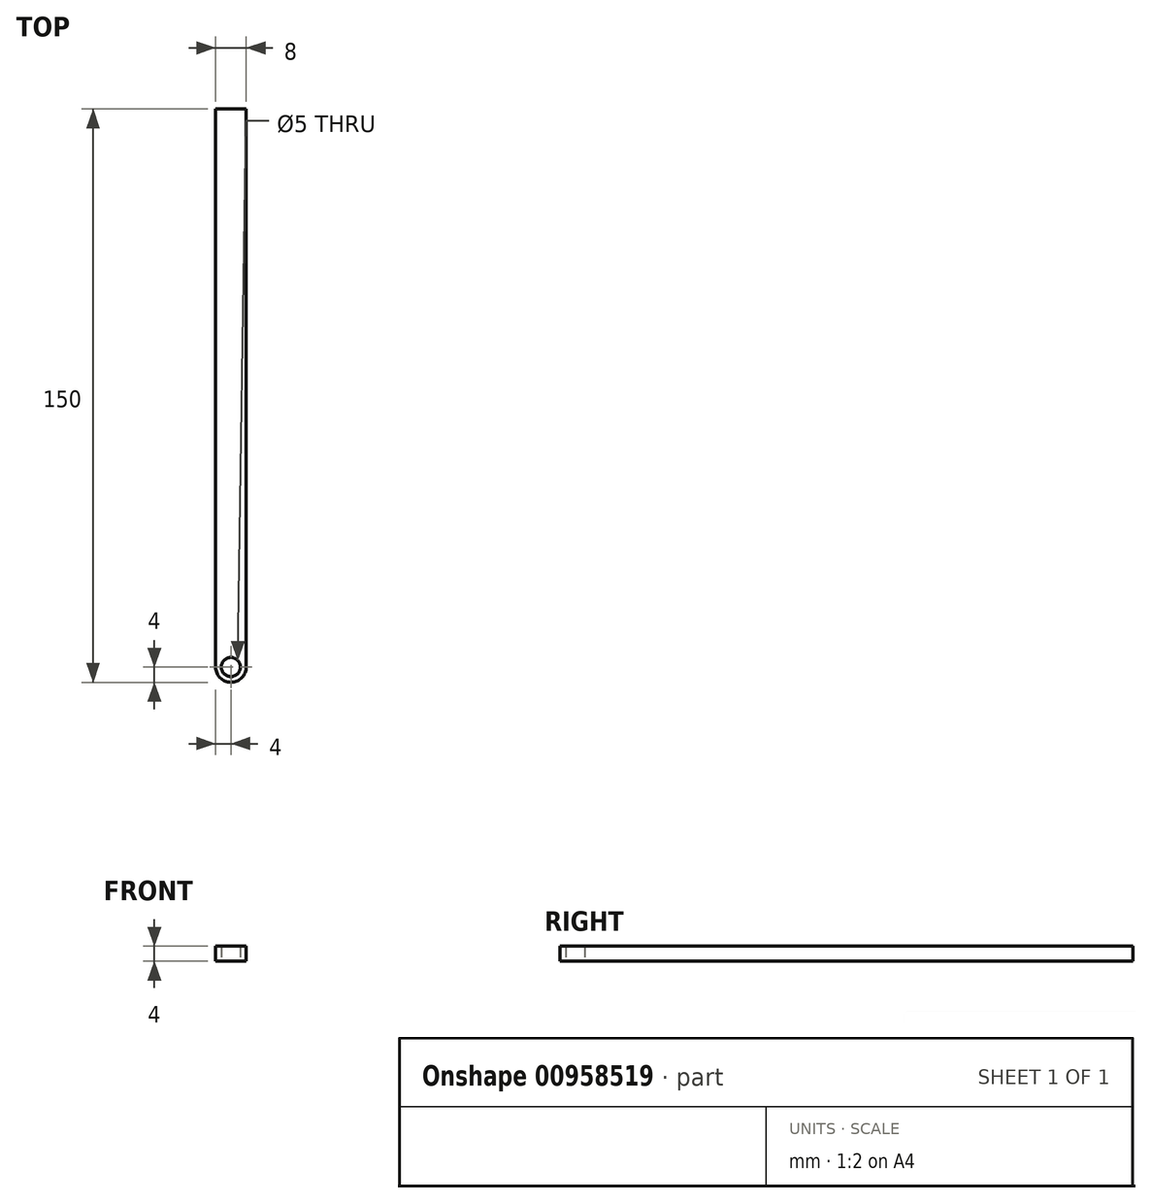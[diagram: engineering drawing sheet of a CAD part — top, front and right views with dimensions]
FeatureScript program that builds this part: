
annotation { "Feature Type Name" : "Feature", "Feature Type Description" : "" }
export const myFeature = defineFeature(function(context is Context, id is Id, definition is map)
    precondition{}
    {
        {
            var Q0;
            Q0=qCreatedBy(makeId("Top.planeOp"),FACE);
            var sketch = newSketch(context, id + "F0", { "sketchPlane" : qUnion([Q0])});
            skLineSegment(sketch, "E0.top", {"start": v(0, 150) * mm, "end": v(8, 150) * mm});
            skLineSegment(sketch, "E0.left", {"start": v(0, 4) * mm, "end": v(0, 150) * mm});
            skLineSegment(sketch, "E0.right", {"start": v(8, 4) * mm, "end": v(8, 150) * mm});
            skArc(sketch, "E1", {"start": v(0, 4) * mm, "mid": v(4, 0) * mm, "end": v(8, 4) * mm});
            skCircle(sketch, "E2", {"center": v(4, 4) * mm, "radius": 2.5 * mm});
            skSolve(sketch);
        }
        {
            var Q0;
            Q0=makeQuery(id+"F0.imprint","IMPRINT",FACE,{"disambiguationData":[TD([[makeQuery(id+"F0.imprint","IMPRINT",EDGE,{"derivedFrom":sQuery(id+"F0.wireOp",EDGE,"E0.top")}),-1.0]])]});
            extrude(context, id + "F1", {"entities" : qUnion([Q0]), "depth" : 4 * mm, "offsetDistance" : 25 * mm});
        }
    });
